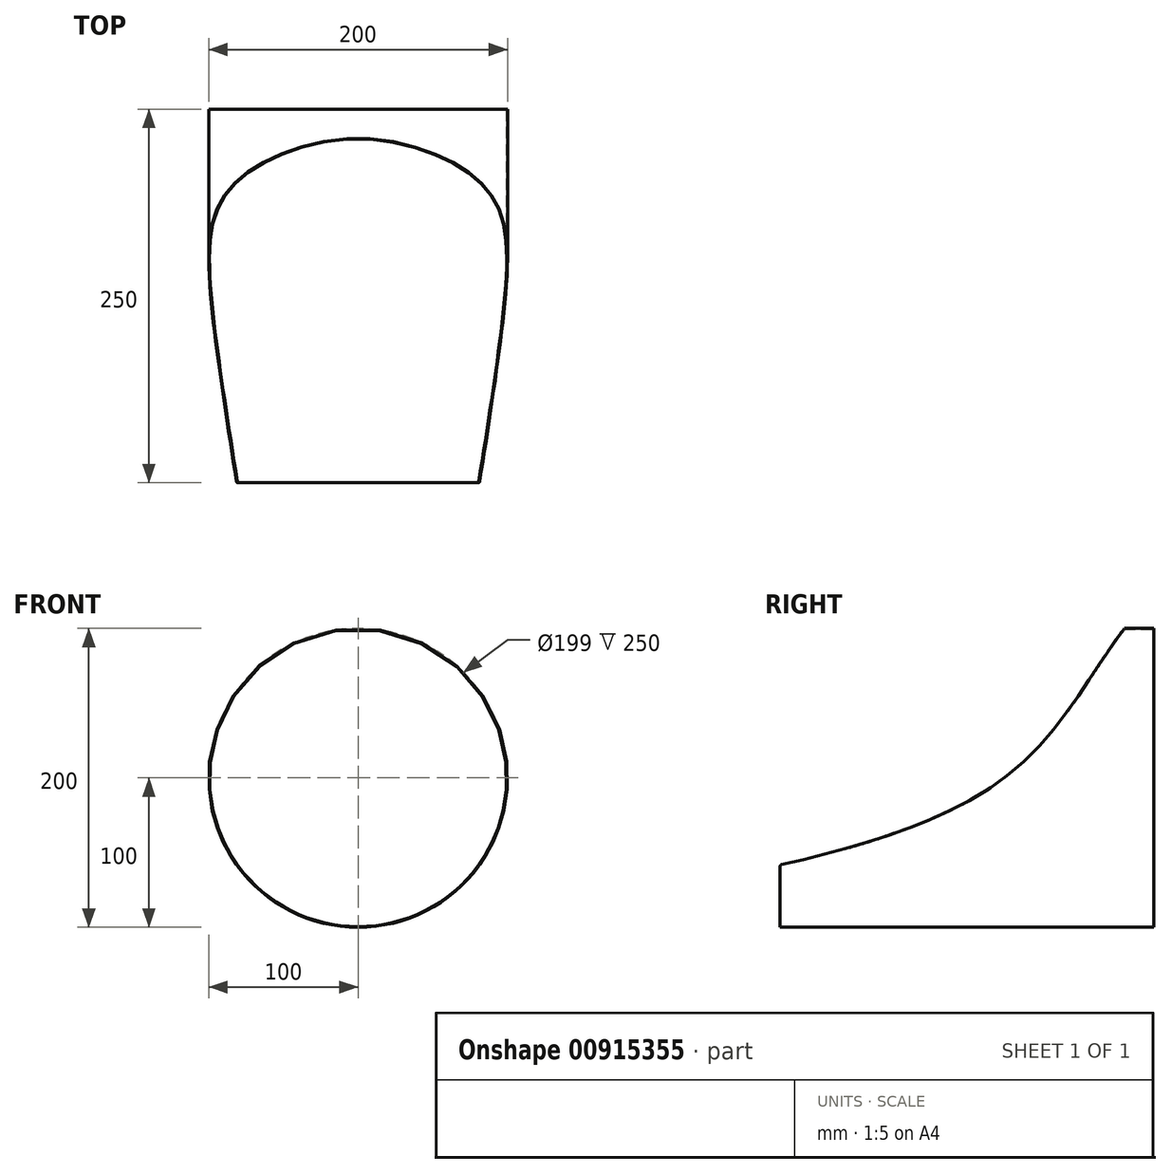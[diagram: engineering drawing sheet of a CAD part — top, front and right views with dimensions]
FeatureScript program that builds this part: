
annotation { "Feature Type Name" : "Feature", "Feature Type Description" : "" }
export const myFeature = defineFeature(function(context is Context, id is Id, definition is map)
    precondition{}
    {
        {
            var Q0;
            Q0=qCreatedBy(makeId("Front.planeOp"),FACE);
            var sketch = newSketch(context, id + "F0", { "sketchPlane" : qUnion([Q0])});
            skCircle(sketch, "E0", {"center": v(0, 0) * mm, "radius": 100 * mm});
            skCircle(sketch, "E1", {"center": v(0, 0) * mm, "radius": 99.5 * mm});
            skSolve(sketch);
        }
        {
            var Q0;
            Q0 = qSketchRegion(id + "F0", true);
            extrude(context, id + "F1", {"entities" : qUnion([Q0]), "depth" : 50 * mm, "offsetDistance" : 25 * mm});
        }
        {
            var Q0;
            Q0=qCreatedBy(makeId("Front.planeOp"),FACE);
            cPlane(context, id + "F2", {"entities" : qUnion([Q0]), "cplaneType" : CPlaneType.OFFSET, "offset" : 50 * mm, "width" : 150 * mm, "height" : 150 * mm});
        }
        {
            var Q0;
            Q0=qCreatedBy(id+"F2.planeOp",FACE);
            var sketch = newSketch(context, id + "F3", { "sketchPlane" : qUnion([Q0])});
            skCircle(sketch, "E2", {"center": v(0, 0) * mm, "radius": 100 * mm});
            skCircle(sketch, "E3", {"center": v(0, 0) * mm, "radius": 99.5 * mm});
            skSolve(sketch);
        }
        {
            var Q0;
            Q0 = qSketchRegion(id + "F3", true);
            extrude(context, id + "F4", {"entities" : qUnion([Q0]), "operationType" : NewBodyOperationType.ADD, "depth" : 200 * mm, "offsetDistance" : 25 * mm});
        }
        {
            var Q0;
            Q0=qCreatedBy(makeId("Right.planeOp"),FACE);
            cPlane(context, id + "F5", {"entities" : qUnion([Q0]), "cplaneType" : CPlaneType.OFFSET, "offset" : 100 * mm, "width" : 150 * mm, "height" : 150 * mm});
        }
        {
            var Q0;
            Q0=qCreatedBy(id+"F5.planeOp",FACE);
            var sketch = newSketch(context, id + "F6", { "sketchPlane" : qUnion([Q0])});
            skFitSpline(sketch, "E4", {"points": [v(-11.54, 109.18) * mm, v(-99.88, 0) * mm, v(-269.2, -62.73) * mm], "startDerivative": vector(-165.6, -172.04) * mm, "endDerivative": vector(-221.25, -51.3) * mm});
            skLineSegment(sketch, "E5", {"start": v(-11.54, 109.18) * mm, "end": v(-268.63, 109.18) * mm});
            skLineSegment(sketch, "E6", {"start": v(-268.63, 109.18) * mm, "end": v(-269.2, -62.73) * mm});
            skArc(sketch, "E7", {"start": v(-249.07, -58.13) * mm, "mid": v(-249.77, -58.54) * mm, "end": v(-250.12, -59.28) * mm});
            skLineSegment(sketch, "E8", {"start": v(-250.12, -59.28) * mm, "end": v(-254.42, -60.66) * mm});
            skLineSegment(sketch, "E9", {"start": v(-269.2, -62.73) * mm, "end": v(-254.42, -60.66) * mm});
            skSolve(sketch);
        }
        {
            var Q0;
            Q0 = qSketchRegion(id + "F6", true);
            extrude(context, id + "F7", {"entities" : qUnion([Q0]), "operationType" : NewBodyOperationType.REMOVE, "oppositeDirection" : true, "depth" : 222 * mm, "offsetDistance" : 25 * mm});
        }
    });
